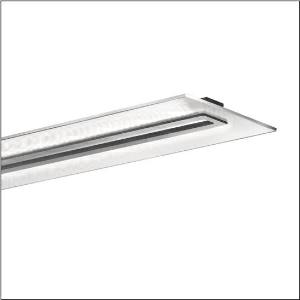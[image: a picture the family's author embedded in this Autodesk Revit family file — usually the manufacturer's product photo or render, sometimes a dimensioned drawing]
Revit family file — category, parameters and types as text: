
# Revit family: vega_r__11_5mn238dle0s3_873d
name_source: partatom
category: Lighting Fixtures
units: mm (PartAtom-declared; Revit-internal decimal feet)

## family parameters
Cut with Voids When Loaded = No
Host = Face
Light Source = No
Part Type = Normal
Room Calculation Point = No
Round Connector Dimension = Use Diameter
Shared = No

## types (1)
- --- (1 x LED 3000K / CRI = 80 (unbekannt), 7300 lm, 3000K)
    Apparent Load = 62 VA
    CIE Flux Codes = 61 86 97 62 100
    Color Rendering = 80
    Color Temperature = 3000K
    Default Elevation = 1800 mm
    Description = Vega® 11, office luminaire, primary light control with prismatic reflector, of PMMA, transparent prismatic structure, CAT 2 (L<= 1500cd/m²), light emission: direct/indirect distribution, primary light characteristic: symmetric, installation type: suspended mounting, surface-mounted, LED, rated luminous flux: 7.300lm, luminous efficacy: 118lm/W, light colour: 830, colour temperature: 3000K, control gear: ECG, with terminal, 3+2-pole, max. 2.5mm², mains connection: 230V, AC, 50Hz, connection cable inclusive, cable length: 1,5m, rated input power: 62W, luminaire housing, rectangular, rounded, of aluminium section, anodised, metallic grey (RAL 9006), length: 1.250mm, width: 350mm, height: 43mm, luminaire housing, lower part, of aluminium section, anodised, metallic grey (RAL 9006), of PC, grey, protection rating (complete): IP20, insulation class (complete): insulation class I (protective earthing), certification: CE, permissible operating ambient temperature: 0..+35°C, standard: EN 50419, packaging unit: 1 piece
    Height = 40 mm  [stored 0.131234 ft]
    Lamp = 1 x LED 3000K / CRI >= 80 (unbekannt)
    Lamp Light Flux = 7300 lm
    Lamp count = 1
    Length = 1250 mm
    Luminous efficacy = 118 lm/W
    Manufacturer = Siteco
    ModVariant = No
    Model = 5MN238DLE0S3
    Mounting Place = Ceiling
    Mounting Type = Pendant
    Number of Poles = 1
    OnlyDefault = Yes
    Power Factor = 1
    Product Name = Vega® 11
    Product group = office luminaire | ceiling pendant
    ProductGroupID = 902
    Protection Class = Protection class I
    Protection Degree = IP 20
    RLX_Detail_Level = 1
    RLX_Emergency_Light_Flux = 0 lm
    RLX_Emergency_Type = 0
    RLX_Emergency_Type_DB = No
    RlxData = <blob elided: 62717 chars, md5=8700da98>
    Socket = socket
    Standby Power = 0 W
    System Light Flux = 7300 lm
    System Power = 62 W
    Type Comments = factory setting: luminous flux: 100 % | dim-lin: 254 | 460 mA
    Type Image = l_1004807.jpg
    URL = http://relux.com
    VarID = @adj_149757
    Voltage = 0 V
    Weight = 0.00 kg
    Width = 350 mm

note: [stored X ft] marks values corroborated as IEEE doubles in the binary element streams (Revit-internal decimal feet)

## geometry (parser evidence)
native form markers: Blend x4, Sweep x12
no freeform markers — native parametric forms only
